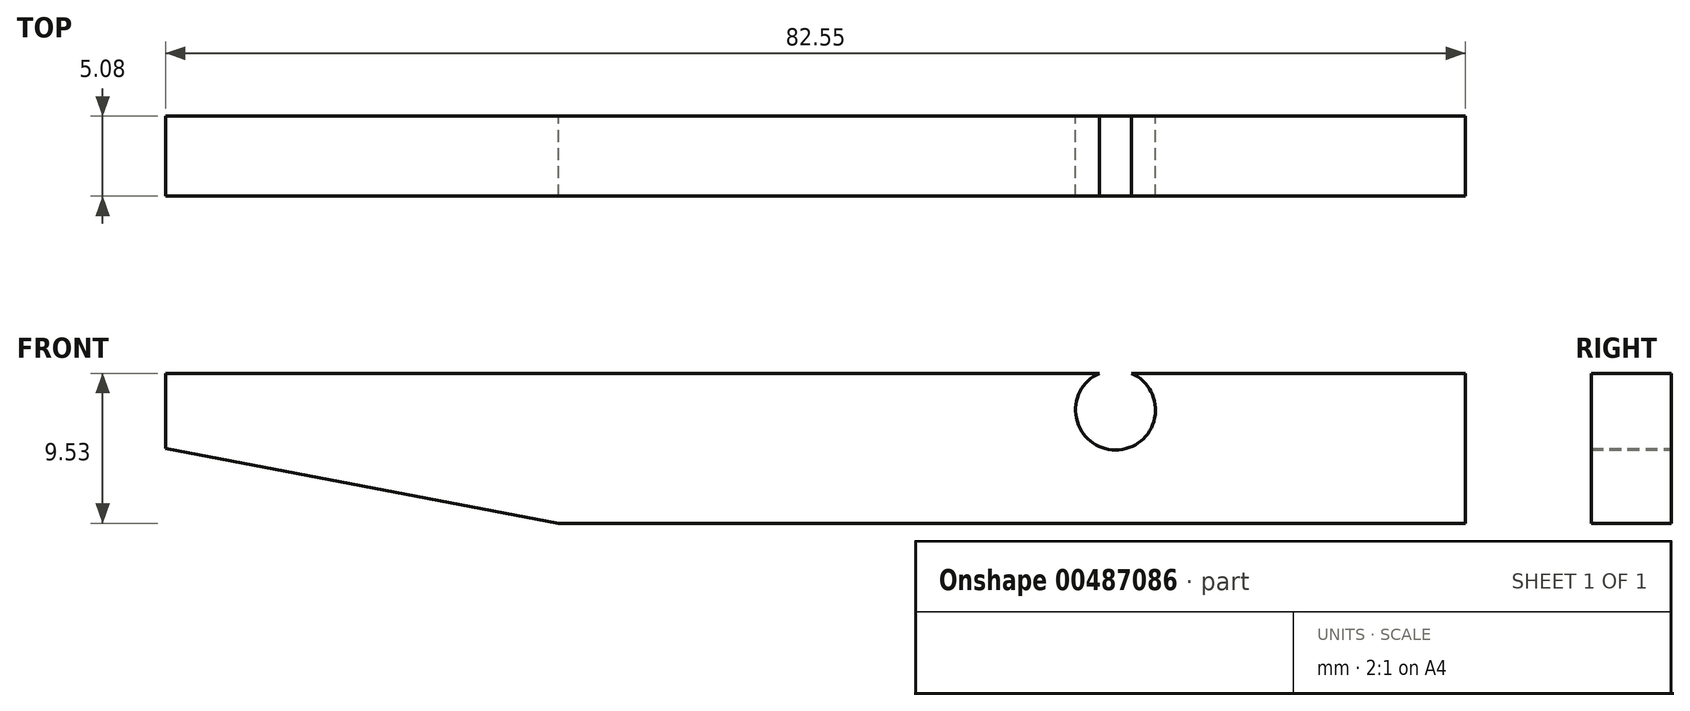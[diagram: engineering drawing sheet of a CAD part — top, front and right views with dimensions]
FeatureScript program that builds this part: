
annotation { "Feature Type Name" : "Feature", "Feature Type Description" : "" }
export const myFeature = defineFeature(function(context is Context, id is Id, definition is map)
    precondition{}
    {
        {
            var Q0;
            Q0=qCreatedBy(makeId("Front.planeOp"),FACE);
            var sketch = newSketch(context, id + "F0", { "sketchPlane" : qUnion([Q0])});
            skLineSegment(sketch, "E0.bottom", {"start": v(-51.24, -8.1) * mm, "end": v(8.07, -8.1) * mm});
            skLineSegment(sketch, "E0.top", {"start": v(-26.29, -17.63) * mm, "end": v(31.31, -17.63) * mm});
            skLineSegment(sketch, "E0.left", {"start": v(-51.24, -8.1) * mm, "end": v(-51.24, -12.87) * mm});
            skLineSegment(sketch, "E0.right", {"start": v(31.31, -8.1) * mm, "end": v(31.31, -17.63) * mm});
            skLineSegment(sketch, "E1", {"start": v(9.09, 0) * mm, "end": v(9.09, -8.1) * mm});
            skLineSegment(sketch, "E2", {"start": v(31.31, -8.1) * mm, "end": v(31.31, 0) * mm});
            skArc(sketch, "E3", {"start": v(8.07, -8.1) * mm, "mid": v(9.09, -12.98) * mm, "end": v(10.1, -8.1) * mm});
            skLineSegment(sketch, "E4.trimOffspring", {"start": v(10.1, -8.1) * mm, "end": v(31.31, -8.1) * mm});
            skLineSegment(sketch, "E5", {"start": v(-51.24, -12.87) * mm, "end": v(-26.29, -17.63) * mm});
            skPoint(sketch, "E6.orphan", {"position": v(-51.24, -17.63) * mm});
            skSolve(sketch);
        }
        {
            var Q0;
            Q0=qSketchRegion(id+"F0",true);
            extrude(context, id + "F1", {"entities" : qUnion([Q0]), "depth" : 5.08 * mm});
        }
    });
